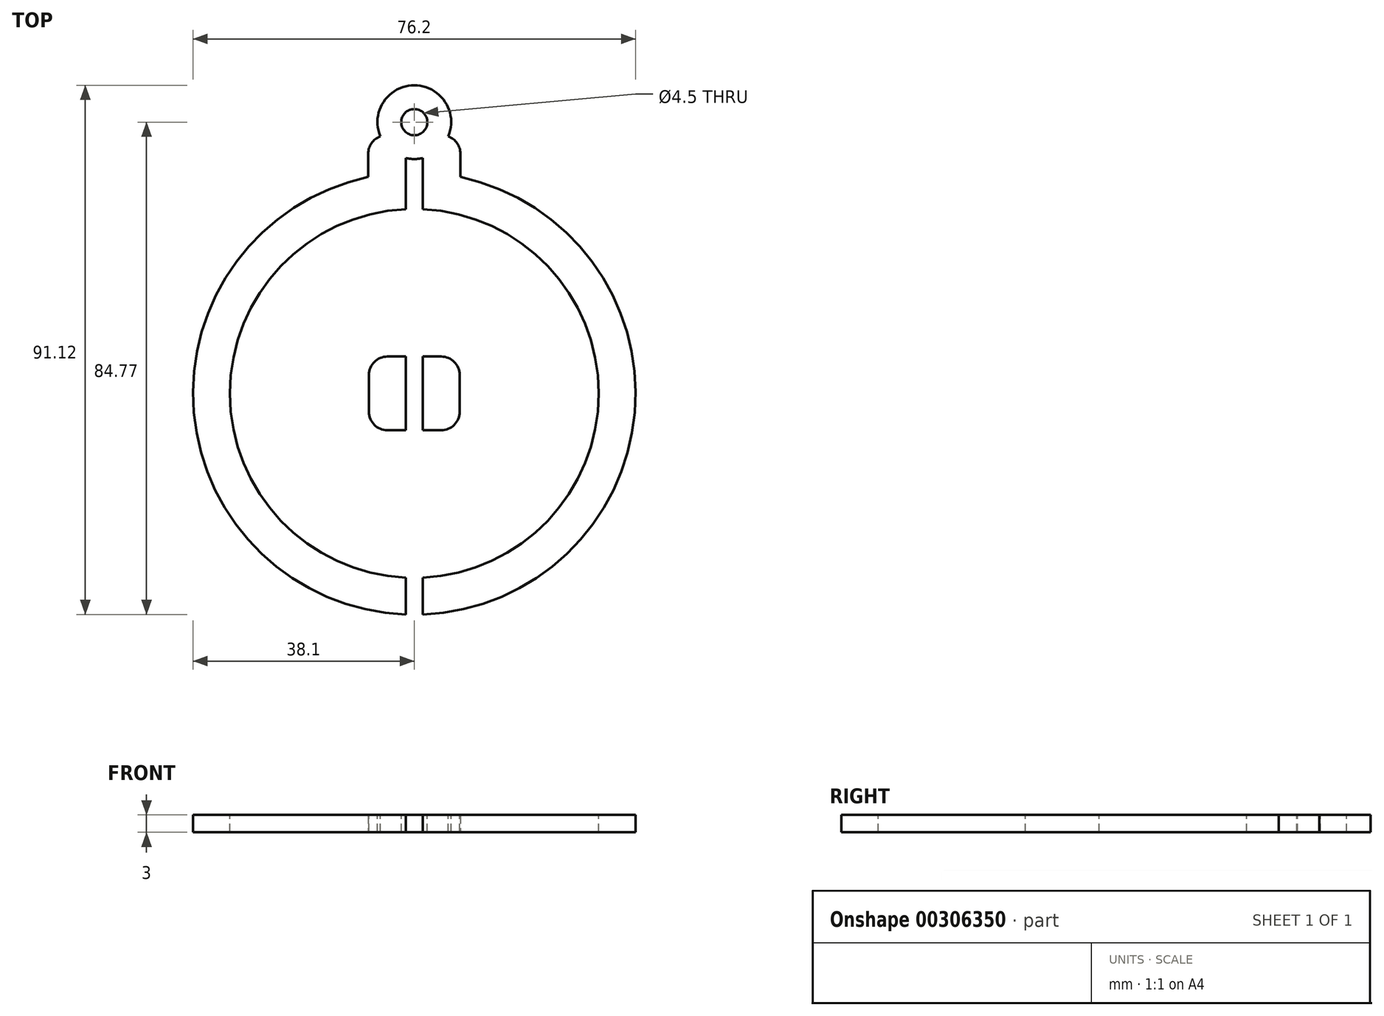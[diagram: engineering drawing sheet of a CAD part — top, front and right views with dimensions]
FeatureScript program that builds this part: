
annotation { "Feature Type Name" : "Feature", "Feature Type Description" : "" }
export const myFeature = defineFeature(function(context is Context, id is Id, definition is map)
    precondition{}
    {
        {
            var Q0;
            Q0=qCreatedBy(makeId("Top.planeOp"),FACE);
            var sketch = newSketch(context, id + "F0", { "sketchPlane" : qUnion([Q0])});
            skArc(sketch, "E0", {"start": v(-7.94, 37.26) * mm, "mid": v(0, -38.1) * mm, "end": v(7.94, 37.26) * mm});
            skLineSegment(sketch, "E1.top", {"start": v(4.76, 44.45) * mm, "end": v(-4.76, 44.45) * mm});
            skLineSegment(sketch, "E1.left", {"start": v(7.94, 37.26) * mm, "end": v(7.94, 41.28) * mm});
            skLineSegment(sketch, "E1.right", {"start": v(-7.94, 37.26) * mm, "end": v(-7.94, 41.28) * mm});
            skPoint(sketch, "E1.middle", {"position": v(0, 38.1) * mm});
            skPoint(sketch, "E2.orphan", {"position": v(-7.94, 31.75) * mm});
            skPoint(sketch, "E3.orphan", {"position": v(7.94, 31.75) * mm});
            skPoint(sketch, "E4.visualSharp", {"position": v(7.94, 44.45) * mm});
            skArc(sketch, "E4.filletArc", {"start": v(7.94, 41.28) * mm, "mid": v(7, 43.52) * mm, "end": v(4.76, 44.45) * mm});
            skPoint(sketch, "E5.visualSharp", {"position": v(-7.94, 44.45) * mm});
            skArc(sketch, "E5.filletArc", {"start": v(-4.76, 44.45) * mm, "mid": v(-7, 43.52) * mm, "end": v(-7.94, 41.28) * mm});
            skSolve(sketch);
        }
        {
            var Q0;
            Q0 = qSketchRegion(id + "F0", true);
            extrude(context, id + "F1", {"entities" : qUnion([Q0]), "depth" : 3 * mm});
        }
        {
            var Q0;
            Q0 = qSketchRegion(id + "F0", true);
            extrude(context, id + "F2", {"entities" : qUnion([Q0]), "depth" : 3 * mm});
        }
        {
            var Q0;
            Q0=makeQuery(id+"F1.opExtrude","CAP_FACE",FACE,{"disambiguationData":[OSD([sQuery(id+"F0.wireOp",EDGE,"E0"),sQuery(id+"F0.wireOp",EDGE,"E1.top"),sQuery(id+"F0.wireOp",EDGE,"E1.left"),sQuery(id+"F0.wireOp",EDGE,"E1.right"),sQuery(id+"F0.wireOp",EDGE,"E4.filletArc"),sQuery(id+"F0.wireOp",EDGE,"E5.filletArc")])],"isStart":false});
            var sketch = newSketch(context, id + "F3", { "sketchPlane" : qUnion([Q0])});
            skLineSegment(sketch, "E6", {"start": v(0, 0) * mm, "end": v(0, 44.45) * mm, "construction": true});
            skLineSegment(sketch, "E7.bottom", {"start": v(-1.45, 44.45) * mm, "end": v(1.45, 44.45) * mm});
            skLineSegment(sketch, "E7.top", {"start": v(-1.45, 0) * mm, "end": v(1.45, 0) * mm});
            skLineSegment(sketch, "E7.left", {"start": v(-1.45, 44.45) * mm, "end": v(-1.45, 0) * mm});
            skLineSegment(sketch, "E7.right", {"start": v(1.45, 44.45) * mm, "end": v(1.45, 0) * mm});
            skSolve(sketch);
        }
        {
            var Q0;
            Q0=makeQuery(id+"F3.imprint","IMPRINT",FACE,{"disambiguationData":[TD([[makeQuery(id+"F3.imprint","IMPRINT",EDGE,{"derivedFrom":sQuery(id+"F3.wireOp",EDGE,"E7.top")}),-1.0]])]});
            var sketch = newSketch(context, id + "F4", { "sketchPlane" : qUnion([Q0])});
            skLineSegment(sketch, "E8", {"start": v(0, 0) * mm, "end": v(0, -10.8) * mm, "construction": true});
            skLineSegment(sketch, "E9.bottom", {"start": v(-1.45, -41.4) * mm, "end": v(1.45, -41.4) * mm});
            skLineSegment(sketch, "E9.top", {"start": v(-1.45, 0) * mm, "end": v(1.45, 0) * mm});
            skLineSegment(sketch, "E9.left", {"start": v(-1.45, -41.4) * mm, "end": v(-1.45, 0) * mm});
            skLineSegment(sketch, "E9.right", {"start": v(1.45, -41.4) * mm, "end": v(1.45, 0) * mm});
            skSolve(sketch);
        }
        {
            var Q0;
            Q0 = qSketchRegion(id + "F3", true);
            extrude(context, id + "F5", {"entities" : qUnion([Q0]), "operationType" : NewBodyOperationType.REMOVE, "endBound" : BoundingType.THROUGH_ALL, "oppositeDirection" : true, "depth" : 25.4 * mm});
        }
        {
            var Q0;
            Q0 = qSketchRegion(id + "F4", true);
            extrude(context, id + "F6", {"entities" : qUnion([Q0]), "operationType" : NewBodyOperationType.REMOVE, "oppositeDirection" : true, "depth" : 25.4 * mm});
        }
        {
            var Q0;
            Q0=makeQuery(id+"F2.opExtrude","CAP_FACE",FACE,{"disambiguationData":[OSD([sQuery(id+"F0.wireOp",EDGE,"E0"),sQuery(id+"F0.wireOp",EDGE,"E1.top"),sQuery(id+"F0.wireOp",EDGE,"E1.left"),sQuery(id+"F0.wireOp",EDGE,"E1.right"),sQuery(id+"F0.wireOp",EDGE,"E4.filletArc"),sQuery(id+"F0.wireOp",EDGE,"E5.filletArc")])],"isStart":false});
            var sketch = newSketch(context, id + "F7", { "sketchPlane" : qUnion([Q0])});
            skCircle(sketch, "E10", {"center": v(0, 46.7) * mm, "radius": 2.25 * mm});
            skPoint(sketch, "E10.centerSnap0", {"position": v(0, 44.45) * mm});
            skCircle(sketch, "E11", {"center": v(0, 46.7) * mm, "radius": 6.35 * mm});
            skSolve(sketch);
        }
        {
            var Q0;
            Q0 = qSketchRegion(id + "F7", true);
            var Q1;
            Q1=makeQuery(id+"F2.opExtrude","SWEPT_BODY",BODY,{"disambiguationData":[OSD([sQuery(id+"F0.wireOp",EDGE,"E0"),sQuery(id+"F0.wireOp",EDGE,"E1.top"),sQuery(id+"F0.wireOp",EDGE,"E1.left"),sQuery(id+"F0.wireOp",EDGE,"E1.right"),sQuery(id+"F0.wireOp",EDGE,"E4.filletArc"),sQuery(id+"F0.wireOp",EDGE,"E5.filletArc")])]});
            extrude(context, id + "F8", {"entities" : qUnion([Q0]), "operationType" : NewBodyOperationType.ADD, "oppositeDirection" : true, "endBoundEntityBody" : qUnion([Q1]), "depth" : 3 * mm});
        }
        {
            var Q0;
            Q0=makeQuery(id+"F8.boolean.opBoolean","MERGE",FACE,{"derivedFrom":[makeQuery(id+"F2.opExtrude","CAP_FACE",FACE,{"disambiguationData":[OSD([sQuery(id+"F0.wireOp",EDGE,"E0"),sQuery(id+"F0.wireOp",EDGE,"E1.top"),sQuery(id+"F0.wireOp",EDGE,"E1.left"),sQuery(id+"F0.wireOp",EDGE,"E1.right"),sQuery(id+"F0.wireOp",EDGE,"E4.filletArc"),sQuery(id+"F0.wireOp",EDGE,"E5.filletArc")])],"isStart":false}),makeQuery(id+"F8.opExtrude","CAP_FACE",FACE,{"disambiguationData":[OSD([sQuery(id+"F7.wireOp",EDGE,"E10"),sQuery(id+"F7.wireOp",EDGE,"E11")])],"isStart":true})]});
            var sketch = newSketch(context, id + "F9", { "sketchPlane" : qUnion([Q0])});
            skArc(sketch, "E12.0", {"start": v(7.8, -30.78) * mm, "mid": v(31.5, 3.93) * mm, "end": v(0, 31.75) * mm});
            skArc(sketch, "E12.1", {"start": v(0, 31.75) * mm, "mid": v(-31.5, 3.93) * mm, "end": v(-7.8, -30.78) * mm});
            skLineSegment(sketch, "E12.2", {"start": v(-7.8, -30.78) * mm, "end": v(-7.8, 3.18) * mm});
            skLineSegment(sketch, "E12.3", {"start": v(-4.63, 6.35) * mm, "end": v(4.62, 6.35) * mm});
            skLineSegment(sketch, "E12.4", {"start": v(7.8, -30.78) * mm, "end": v(7.8, 3.18) * mm});
            skPoint(sketch, "E13.visualSharp", {"position": v(-7.8, 6.35) * mm});
            skArc(sketch, "E13.filletArc", {"start": v(-4.63, 6.35) * mm, "mid": v(-6.87, 5.42) * mm, "end": v(-7.8, 3.18) * mm});
            skPoint(sketch, "E14.visualSharp", {"position": v(7.8, 6.35) * mm});
            skArc(sketch, "E14.filletArc", {"start": v(7.8, 3.18) * mm, "mid": v(6.87, 5.42) * mm, "end": v(4.62, 6.35) * mm});
            skSolve(sketch);
        }
        {
            var Q0;
            Q0 = qSketchRegion(id + "F9", true);
            extrude(context, id + "F10", {"entities" : qUnion([Q0]), "operationType" : NewBodyOperationType.REMOVE, "oppositeDirection" : true, "depth" : 25.4 * mm});
        }
        {
            var Q0;
            Q0=makeQuery(id+"F1.opExtrude","CAP_FACE",FACE,{"disambiguationData":[OSD([sQuery(id+"F0.wireOp",EDGE,"E0"),sQuery(id+"F0.wireOp",EDGE,"E1.top"),sQuery(id+"F0.wireOp",EDGE,"E1.left"),sQuery(id+"F0.wireOp",EDGE,"E1.right"),sQuery(id+"F0.wireOp",EDGE,"E4.filletArc"),sQuery(id+"F0.wireOp",EDGE,"E5.filletArc")])],"isStart":false});
            var sketch = newSketch(context, id + "F11", { "sketchPlane" : qUnion([Q0])});
            skArc(sketch, "E15.0", {"start": v(-7.8, 30.78) * mm, "mid": v(0, -31.75) * mm, "end": v(7.8, 30.78) * mm});
            skLineSegment(sketch, "E16.0", {"start": v(7.8, 30.78) * mm, "end": v(7.8, -3.18) * mm});
            skLineSegment(sketch, "E16.1", {"start": v(-4.63, -6.35) * mm, "end": v(4.62, -6.35) * mm});
            skLineSegment(sketch, "E16.2", {"start": v(-7.8, 30.78) * mm, "end": v(-7.8, -3.18) * mm});
            skPoint(sketch, "E17.visualSharp", {"position": v(-7.8, -6.35) * mm});
            skArc(sketch, "E17.filletArc", {"start": v(-7.8, -3.18) * mm, "mid": v(-6.87, -5.42) * mm, "end": v(-4.63, -6.35) * mm});
            skPoint(sketch, "E18.visualSharp", {"position": v(7.8, -6.35) * mm});
            skArc(sketch, "E18.filletArc", {"start": v(4.62, -6.35) * mm, "mid": v(6.87, -5.42) * mm, "end": v(7.8, -3.18) * mm});
            skSolve(sketch);
        }
        {
            var Q0;
            Q0 = qSketchRegion(id + "F11", true);
            extrude(context, id + "F12", {"entities" : qUnion([Q0]), "operationType" : NewBodyOperationType.REMOVE, "oppositeDirection" : true, "depth" : 25.4 * mm});
        }
    });
